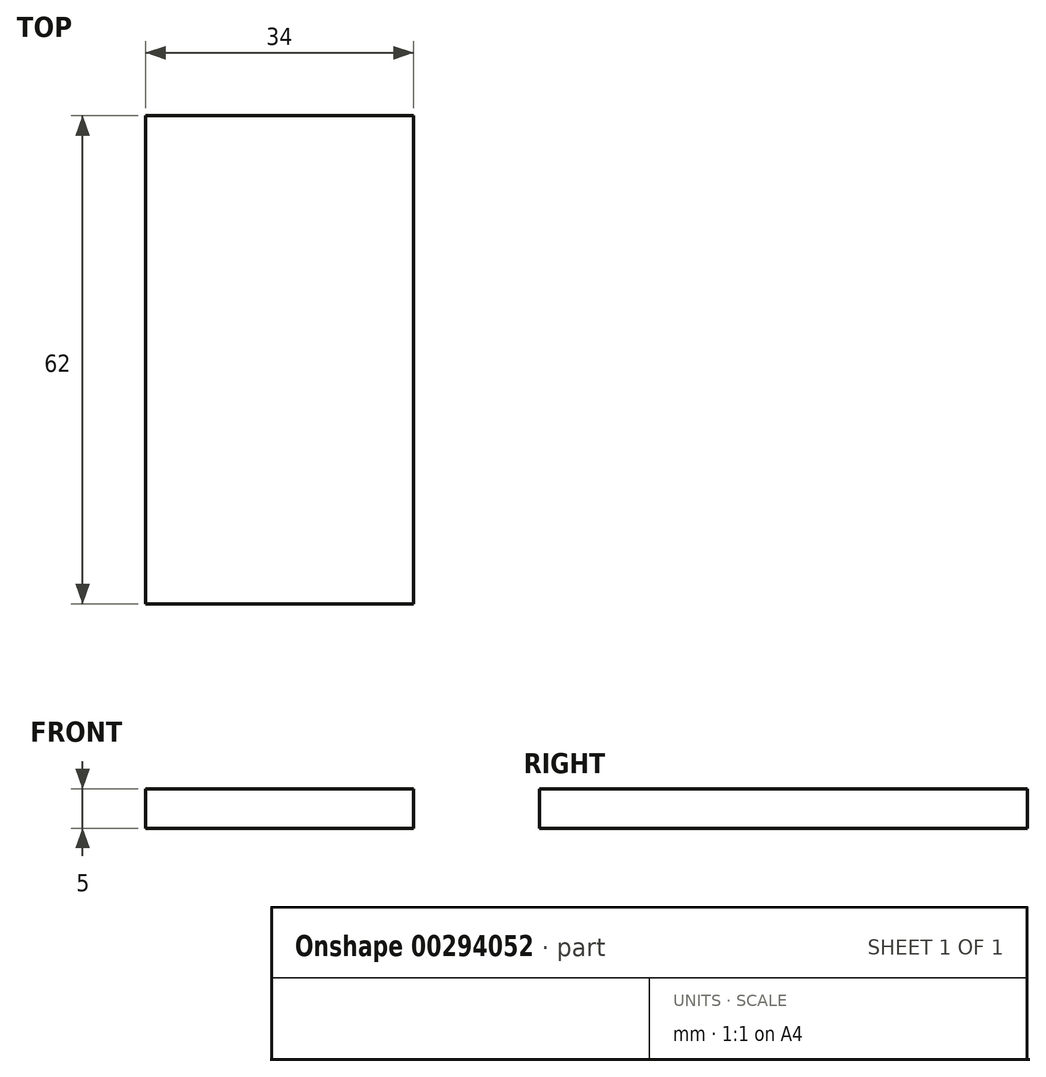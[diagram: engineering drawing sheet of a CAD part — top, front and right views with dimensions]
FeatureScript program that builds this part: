
annotation { "Feature Type Name" : "Feature", "Feature Type Description" : "" }
export const myFeature = defineFeature(function(context is Context, id is Id, definition is map)
    precondition{}
    {
        {
            var Q0;
            Q0=qCreatedBy(makeId("Top.planeOp"),FACE);
            var sketch = newSketch(context, id + "F0", { "sketchPlane" : qUnion([Q0])});
            skLineSegment(sketch, "E0.bottom", {"start": v(-17, 31) * mm, "end": v(17, 31) * mm});
            skLineSegment(sketch, "E0.top", {"start": v(-17, -31) * mm, "end": v(17, -31) * mm});
            skLineSegment(sketch, "E0.left", {"start": v(-17, 31) * mm, "end": v(-17, -31) * mm});
            skLineSegment(sketch, "E0.right", {"start": v(17, 31) * mm, "end": v(17, -31) * mm});
            skPoint(sketch, "E0.middle", {"position": v(0, 0) * mm});
            skSolve(sketch);
        }
        {
            var Q0;
            Q0=qSketchRegion(id+"F0",true);
            extrude(context, id + "F1", {"entities" : qUnion([Q0]), "depth" : 5 * mm});
        }
    });
